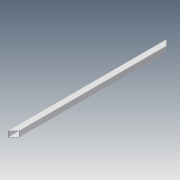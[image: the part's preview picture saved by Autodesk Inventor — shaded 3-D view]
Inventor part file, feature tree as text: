
AUTODESK INVENTOR PART (.ipt)
format: ipt  version: 2014 (Build 180170000, 170)  size: 108,032 bytes
history: native  units: in
note: dims shown in document units (in); Inventor stores cm internally (conversion verified against a paired STEP export)
features: extrude x2, sketch x2
ambient origin geometry x8: Origin, YZ Plane, XZ Plane, XY Plane, X Axis, Y Axis, Z Axis, Center Point
bodies: Solid1 (feature_tree)
feature tree (4):
  extrude  "Extrusion1"  Depth=1.0in
  extrude  "Extrusion2"  Depth=0.063in
  sketch  "Sketch1"  dims[d0=1.0in d1=1.0in]
  sketch  "Sketch2"  dims[d2=0.07in d3=0.063in d4=27.0in d5=0.0in d7=45.0deg d9=45.0deg d10=1.0in d11=0.0in]
